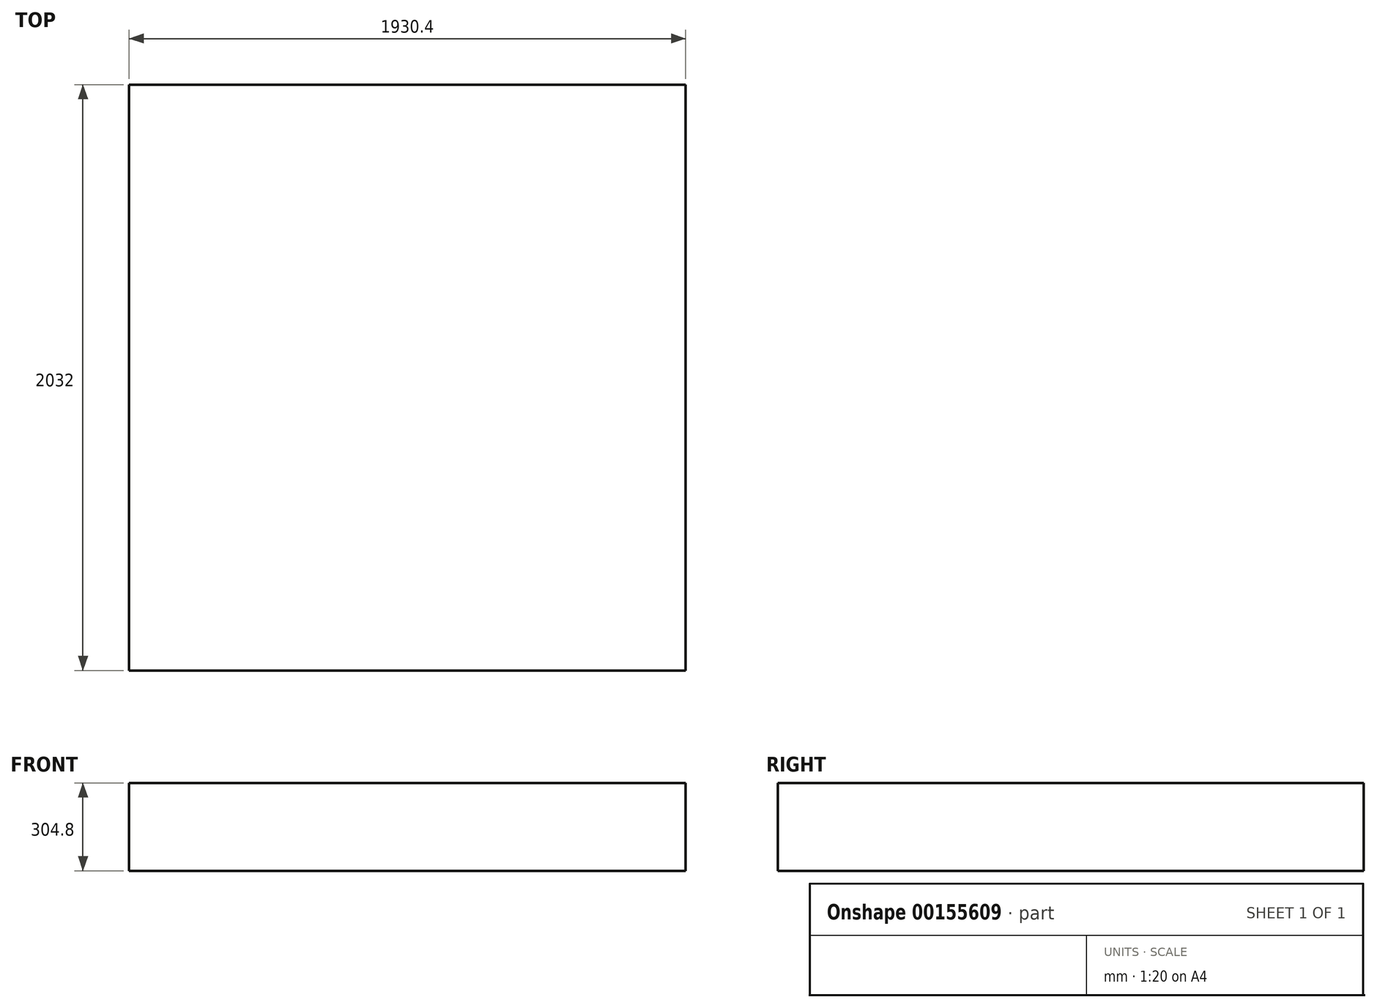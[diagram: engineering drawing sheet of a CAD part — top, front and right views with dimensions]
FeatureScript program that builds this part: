
annotation { "Feature Type Name" : "Feature", "Feature Type Description" : "" }
export const myFeature = defineFeature(function(context is Context, id is Id, definition is map)
    precondition{}
    {
        {
            var Q0;
            Q0=qCreatedBy(makeId("Top.planeOp"),FACE);
            var sketch = newSketch(context, id + "F0", { "sketchPlane" : qUnion([Q0])});
            skLineSegment(sketch, "E0.bottom", {"start": v(965.2, -1016) * mm, "end": v(-965.2, -1016) * mm});
            skLineSegment(sketch, "E0.top", {"start": v(965.2, 1016) * mm, "end": v(-965.2, 1016) * mm});
            skLineSegment(sketch, "E0.left", {"start": v(965.2, -1016) * mm, "end": v(965.2, 1016) * mm});
            skLineSegment(sketch, "E0.right", {"start": v(-965.2, -1016) * mm, "end": v(-965.2, 1016) * mm});
            skPoint(sketch, "E0.middle", {"position": v(0, 0) * mm});
            skSolve(sketch);
        }
        {
            var Q0;
            Q0=makeQuery(id+"F0.imprint","IMPRINT",FACE,{"disambiguationData":[TD([[makeQuery(id+"F0.imprint","IMPRINT",EDGE,{"derivedFrom":sQuery(id+"F0.wireOp",EDGE,"E0.bottom")}),-1.0]])]});
            extrude(context, id + "F1", {"entities" : qUnion([Q0]), "depth" : 304.8 * mm});
        }
    });
